# Revit family: Camera-Security-Panasonic-Super_Dynamic-H265_AI_Engine_Dome-Network-WV-S2136LSeriesX
name_source: partatom
category: Security Devices
units: mm (PartAtom-declared; Revit-internal decimal feet)

## family parameters
Cut with Voids When Loaded = No
Host = Face
Maintain Annotation Orientation = No
OmniClass Number = 23.85.10.14.11
OmniClass Title = Cameras
Part Type = Normal
Room Calculation Point = No
Round Connector Dimension = Use Diameter
Shared = No

## types (2) — shared parameters
Alarm Input Or Output Specification = ALARM IN 1 (Black & white input, Auto time adjustment input) (x1), ALARM IN 2 (ALARM OUT) (x1), ALARM IN 3 (AUX OUT) (x1)
Angle Of View = 115
Audio In = ø3.5 mm stereo mini jack
Audio Out = ø3.5 mm stereo mini jack (monaural output)
Communication Ports = 10Base-T / 100Base-TX, RJ45 connector
Date Last Modified = 2021/04/09
Day Or Night = Yes
Diameter = 5.098 "
Equipment Abbreviation = SC
Family Version = 1.0.0
HFOV Max 169 = 115.00°
HFOV Max 43 = 82.00°
HFOV Min 169 = 36.00°
HFOV Min 43 = 28.00°
Has POE = Yes
Height = 3.976 "
IP Or Analog = IP
Indoor Or Outdoor = Indoor
Manufacturer = Panasonic
Minimum Illumination = 0.007 lx
Model Disclaimer = Contact Panasonic for more information
Mounting Positions = Surface Mount or Mount Dependent
Operational Humidity = 10 to 90 % (no condensation)
Operational Temperature = -10 °C to +50 °C (14 °F to 122 °F)
Pan Max = 120.00°
Pan Min = -240.00°
Panning Range = -240 to +120
Product Documentation Link = https://bizpartner.panasonic.net
Product Material = Paint - Panasonic -i-Pro White
Product Page URL = https://security.panasonic.com
Provide Feedback = https://www.surveymonkey.com
Regulatory Compliance = UL (UL60950-1), c-UL (CSA C22.2 No.60950-1), CE, IEC60950-1, FCC (Part15 ClassA), ICES003 ClassA, EN55032 ClassB, EN55035
Storage Temperature = -10 °C to +50 °C (14 °F to 122 °F)
Tilt Max = 85.00°
Tilt Min = -30.00°
Tilting Range = -30 to +85
URL = http://security.panasonic.com
VFOV Max 169 = 61.00°
VFOV Max 43 = 61.00°
VFOV Min 169 = 20.00°
VFOV Min 43 = 20.00°
Vandal Resistant = No
Weight = 1.04 lb
Wide Dynamic Range = Yes
Yaw Max = 100.00°
Yaw Min = -100.00°
Yawing Range = -100 to +100
z Base Height = 2.118 "
z Base Radius = 2.549 "
z Camera Resolution Type = 1
z Const Pan Handle Length = 19.488 "
z Const Tilt Base Length = 9.843 "
z Const Tilt Base2 Length = 19.685 "
z Const Tilt Handle Length = 11.811 "
z Const Yaw Base Length = 10.236 "
z Const Yaw Base2 Length = 17.323 "
z Const Yaw Handle Length = 9.252 "
z Dome Material = Glass - Panasonic - Smoked
z Type = 2
z VV Face Radius = 4.626 "
z VV Origin Height Offset = 0.303 "
z VV Viewpoint Depth Max = 1.283 "
z VV Viewpoint Depth Min = 1.283 "
zero-valued in all types: Default Elevation, z Zero

## per-type parameters (varying)
| type | Description | Part Description | z Camera Type |
| WV-S2136 | Security Camera, H.265 Fixed Dome, Network, Super Dynamic FullHD, AI Engine, WV-S2136 | Security Camera, H.265 Fixed Dome, Network, Super Dynamic FullHD, AI Engine, WV-S2136 | 21361 |
| WV-S2136L | Security Camera, H.265 Fixed Dome, Network, Super Dynamic FullHD, AI Engine, WV-S2136L | Security Camera, H.265 Fixed Dome, Network, Super Dynamic FullHD, AI Engine, WV-S2136L | 21362 |

note: column(s) folded — value = type name in every type: Model, Part Number

## geometry (parser evidence)
native form markers: Blend x2, Sweep x5
no freeform markers — native parametric forms only
